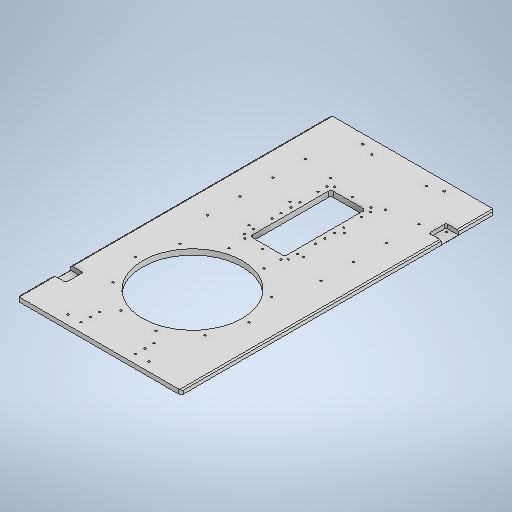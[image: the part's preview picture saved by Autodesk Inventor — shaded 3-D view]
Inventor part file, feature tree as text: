
AUTODESK INVENTOR PART (.ipt)
format: ipt  version: 2025 (Build 290162000, 162)  size: 540,672 bytes
history: native  units: in
note: dims shown in document units (in); Inventor stores cm internally (conversion verified against a paired STEP export)
features: sketch x17, extrude x6, hole x5, fillet x3, chamfer x3, plane x2
ambient origin geometry x8: Origin, YZ Plane, XZ Plane, XY Plane, X Axis, Y Axis, Z Axis, Center Point
bodies: Solid1 (feature_tree)
feature tree (36):
  extrude  "Base Cover"  Depth=27.1654in
  sketch  "Sketch2"  dims[d5=8.6614in d6=0.0in d7=0.0in]
  extrude  "Cylinder Hole"  Depth=0.4724in
  plane  "Work Plane1"
  hole  "Hole3"  [1 undecoded]
  sketch  "Sketch7"  dims[d69=0.1575in d70=3.937in d72=360.0deg]
  plane  "Work Plane2"
  hole  "Hole4"  [1 undecoded]
  sketch  "Sketch9"  dims[d82=1.063in]
  fillet  "Rounded Side Corners"  Radius=7.0625in
  chamfer  "Chamfer1"  Distance=3.937in Angle=360.0deg
  chamfer  "Chamfer2"  Distance=0.1969in
  extrude  "Magnet Seats"  Depth=0.3937in TaperAngle=45.0deg
  hole  "Hole5"  [1 undecoded]
  chamfer  "Chamfer5"  Distance=0.1181in
  hole  "Hole6"  [1 undecoded]
  sketch  "Sketch15"  dims[d85=1.4961in]
  extrude  "Extrusion11"  Depth=0.3937in TaperAngle=0.0deg
  fillet  "Fillet3"  Radius=0.748in
  hole  "Hole7"  [1 undecoded]
  fillet  "Rounded Bottom Corners"  Radius=0.8661in
  extrude  "Extrusion14"  Depth=0.3937in
  extrude  "Extrusion15"  Depth=0.3937in
  sketch  "Sketch1"  dims[d0=14.1732in d1=27.1654in]
  sketch  "Sketch6"  dims[d68=9.8425in]
  sketch  "Sketch8"  dims[d74=0.1628in d75=0.3937in d76=0.1575in d77=0.0787in d78=90.0deg d79=0.3937in d80=0.8108in]
  sketch  "Sketch Circular Pattern4"  dims[d57=0.1936in d58=0.1969in d59=0.1575in d60=0.0787in d61=90.0deg d62=0.1969in d63=0.8108in]
  sketch  "Sketch11"  dims[d83=1.063in]
  sketch  "Sketch12"  dims[d84=1.4961in]
  sketch  "Sketch Rectangular Pattern1"  dims[d2=0.4724in d3=0.0in d4=8.0709in]
  sketch  "Sketch Rectangular Pattern2"  dims[d8=10.6299in d50=5.9055in d55=7.0625in]
  sketch  "Sketch Rectangular Pattern3"  dims[d56=25.5906in]
  sketch  "Sketch Rectangular Pattern4"  dims[d64=10.3543in]
  sketch  "Sketch Rectangular Pattern5"  dims[d65=10.6299in]
  sketch  "Sketch18"  dims[d86=3.1102in]
  sketch  "Sketch19"  dims[d87=3.1102in d88=0.1969in d89=0.0984in d90=0.0787in d91=45.0deg d92=0.0984in d93=0.0787in d94=45.0deg d95=0.1181in d96=0.1181in d97=0.3543in d98=0.0in d109=0.748in d110=0.315in d111=0.8661in d112=0.748in d113=0.1299in d114=0.1299in d115=0.1299in d116=0.1299in d118=0.315in d119=0.8661in d120=0.748in d121=0.748in d122=0.1276in d123=0.315in d124=0.1575in d125=0.0787in d126=90.0deg d127=0.315in d128=0.8108in d129=0.0138in d130=0.0787in d131=45.0deg d146=3.9469in d147=0.7874in d148=0.3937in d149=0.1575in d150=3.937in d152=1.1811in d153=0.3937in d155=0.3937in d157=0.1575in d158=1.1811in d160=0.7874in d161=0.3937in d163=0.3937in d165=9.8425in d166=0.1575in d167=2.9528in d168=1.1811in d169=3.1496in d171=1.4173in d172=0.3937in d174=0.3937in d176=0.1628in d177=0.3937in d178=0.1575in d179=0.0787in d180=90.0deg d181=0.3937in d182=0.8108in d191=3.0in d192=7.0in d193=6.4961in d194=0.8312in d195=0.0in d196=0.1969in d197=0.3937in d198=0.1969in d199=1.9685in d201=0.7874in d202=0.3937in d204=0.3937in d206=0.3189in d207=0.1969in d208=0.3189in d209=1.9685in d211=0.7874in d212=0.3937in d214=0.3937in d216=0.1628in d217=0.3937in d218=0.1575in d219=0.0787in d220=90.0deg d221=0.3937in d222=0.8108in d230=0.2756in d243=0.1378in d244=0.0787in d245=0.3848in d246=0.0in d247=0.1378in d248=0.0787in d249=0.3937in d250=0.0in d26=0.0394in d27=0.0394in d28=0.0394in d29=0.0059in d30=0.0098in d31=0.0148in d32=0.5635in d33=0.0295in d34=0.8108in d35=0.0025in d36=0.0295in d37=0.0148in d66=0.0197in d67=0.0344in]
note: 5 required parameter values undecoded (feature->parameter linkage not recoverable at this tier; creation-order binding heuristic only, values carry confidence <= 0.55)
